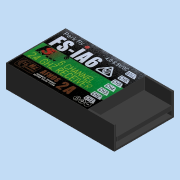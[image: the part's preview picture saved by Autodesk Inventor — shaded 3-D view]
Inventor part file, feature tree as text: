
AUTODESK INVENTOR PART (.ipt)
format: ipt  version: 2022.3 (Build 263350030, 350C)  size: 3,558,912 bytes
history: native  units: in
note: dims shown in document units (in); Inventor stores cm internally (conversion verified against a paired STEP export)
features: sketch x5, extrude x3, other x2, hole x1
ambient origin geometry x8: Origin, YZ Plane, XZ Plane, XY Plane, X Axis, Y Axis, Z Axis, Center Point
bodies: Solid1 (feature_tree)
feature tree (11):
  extrude  "Extrusion1"  Depth=0.8661in
  extrude  "Extrusion2"  Depth=0.3937in
  extrude  "Extrusion3"  Depth=0.063in
  hole  "Hole1"  [1 undecoded]
  other  "Decal1"
  sketch  "Sketch1"  dims[d0=1.5748in d1=0.8661in]
  sketch  "Sketch2"  dims[d2=0.3346in d3=0.0in d6=0.3937in]
  sketch  "Sketch3"  dims[d7=0.3091in d8=0.0in d9=0.063in]
  sketch  "Sketch4"  dims[d10=0.0787in d11=0.4924in d12=0.0in]
  sketch  "Sketch5"  dims[d13=0.0984in d15=0.0394in d16=0.75in d17=0.375in d18=0.25in d19=0.5635in d20=0.031in d21=0.0in d23=0.0256in d24=0.0256in d25=0.7874in d26=0.15in]
  other  "Image8"
note: 1 required parameter value undecoded (feature->parameter linkage not recoverable at this tier; creation-order binding heuristic only, values carry confidence <= 0.55)
